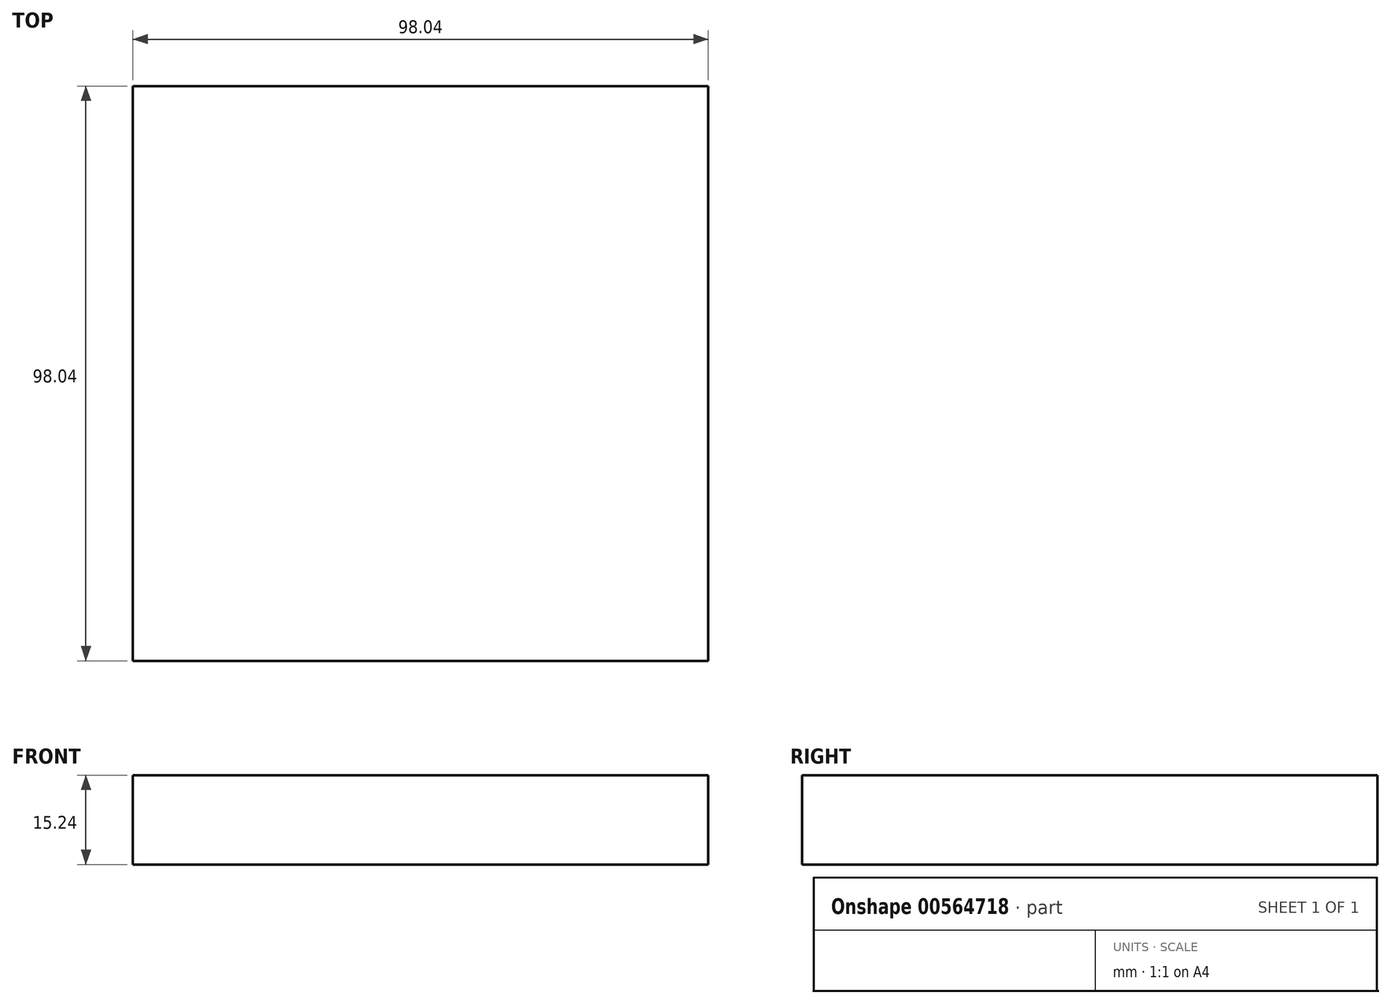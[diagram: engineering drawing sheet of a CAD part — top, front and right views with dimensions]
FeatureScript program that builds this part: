
annotation { "Feature Type Name" : "Feature", "Feature Type Description" : "" }
export const myFeature = defineFeature(function(context is Context, id is Id, definition is map)
    precondition{}
    {
        {
            var Q0;
            Q0=qCreatedBy(makeId("Top.planeOp"),FACE);
            var sketch = newSketch(context, id + "F0", { "sketchPlane" : qUnion([Q0])});
            skPoint(sketch, "E0.middle", {"position": v(0, 0) * mm});
            skLineSegment(sketch, "E1.bottom", {"start": v(-49.02, -49.02) * mm, "end": v(49.02, -49.02) * mm});
            skLineSegment(sketch, "E1.top", {"start": v(-49.02, 49.02) * mm, "end": v(49.02, 49.02) * mm});
            skLineSegment(sketch, "E1.left", {"start": v(-49.02, -49.02) * mm, "end": v(-49.02, 49.02) * mm});
            skLineSegment(sketch, "E1.right", {"start": v(49.02, -49.02) * mm, "end": v(49.02, 49.02) * mm});
            skSolve(sketch);
        }
        {
            var Q0;
            Q0=makeQuery(id+"F0.imprint","IMPRINT",FACE,{"disambiguationData":[TD([[makeQuery(id+"F0.imprint","IMPRINT",EDGE,{"derivedFrom":sQuery(id+"F0.wireOp",EDGE,"E1.bottom")}),1.0]])]});
            extrude(context, id + "F1", {"entities" : qUnion([Q0]), "depth" : 15.24 * mm, "offsetDistance" : 25.4 * mm});
        }
    });
